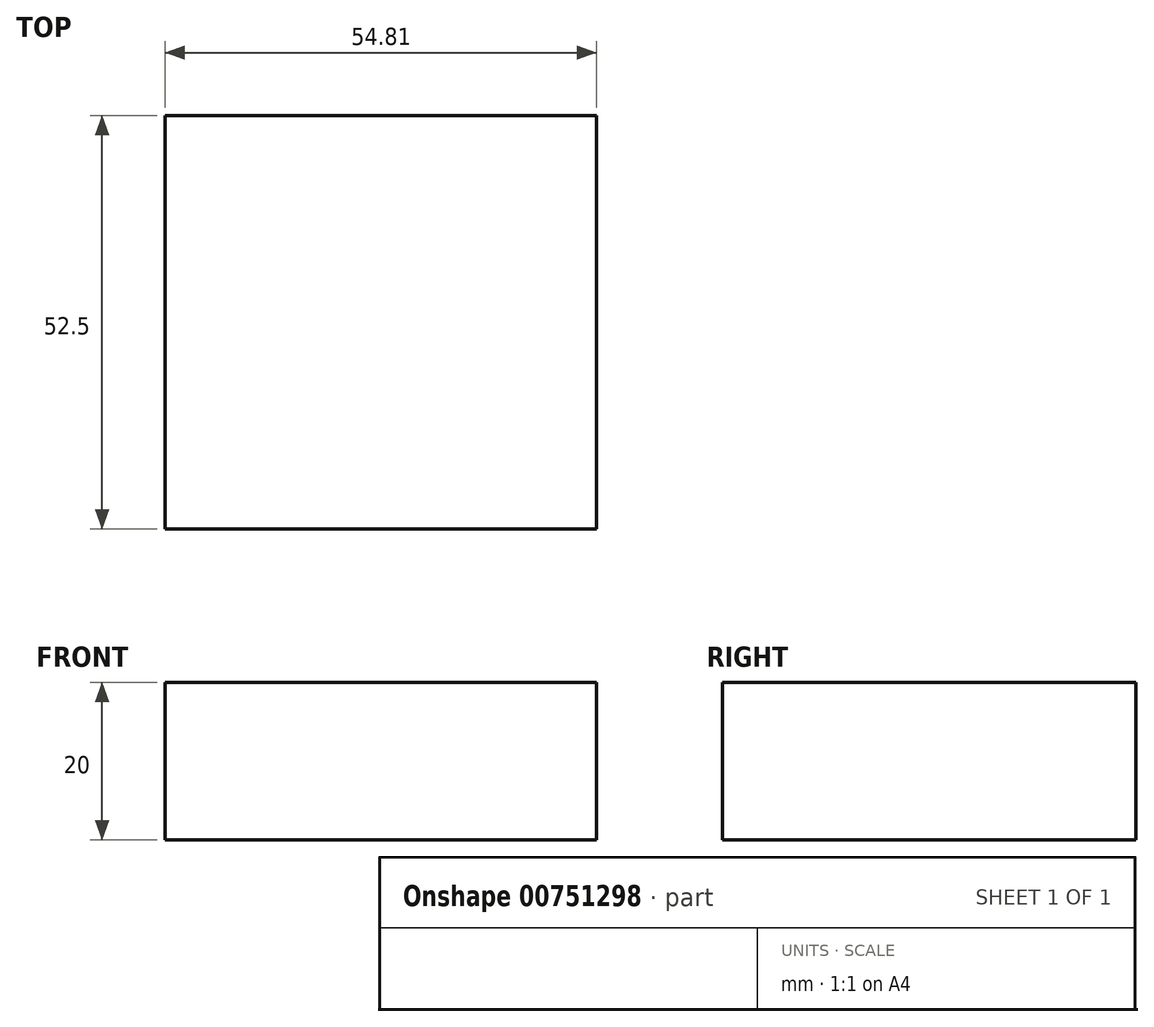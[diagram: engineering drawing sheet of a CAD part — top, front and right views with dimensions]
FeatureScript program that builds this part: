
annotation { "Feature Type Name" : "Feature", "Feature Type Description" : "" }
export const myFeature = defineFeature(function(context is Context, id is Id, definition is map)
    precondition{}
    {
        {
            var Q0;
            Q0=qCreatedBy(makeId("Top.planeOp"),FACE);
            var sketch = newSketch(context, id + "F0", { "sketchPlane" : qUnion([Q0])});
            skLineSegment(sketch, "E0.bottom", {"start": v(-27.39, -32.74) * mm, "end": v(27.42, -32.74) * mm});
            skLineSegment(sketch, "E0.top", {"start": v(-27.39, 19.76) * mm, "end": v(27.42, 19.76) * mm});
            skLineSegment(sketch, "E0.left", {"start": v(-27.39, -32.74) * mm, "end": v(-27.39, 19.76) * mm});
            skLineSegment(sketch, "E0.right", {"start": v(27.42, -32.74) * mm, "end": v(27.42, 19.76) * mm});
            skSolve(sketch);
        }
        {
            var Q0;
            Q0=makeQuery(id+"F0.imprint","IMPRINT",FACE,{"disambiguationData":[TD([[makeQuery(id+"F0.imprint","IMPRINT",EDGE,{"derivedFrom":sQuery(id+"F0.wireOp",EDGE,"E0.bottom")}),1.0]])]});
            extrude(context, id + "F1", {"entities" : qUnion([Q0]), "depth" : 20 * mm, "offsetDistance" : 25.4 * mm});
        }
    });
